# Revit family: PRD_AR_ShwrMxrs_SelfClosingShowerValve_F3SM2004
name_source: partatom
category: Plumbing Fixtures
revit_build: Autodesk Revit 2018 (Build: 20190510_1515(x64)
units: mm (PartAtom-declared; Revit-internal decimal feet)

## family parameters
Cut with Voids When Loaded = Yes
Host = Face
OmniClass Number = 23.45.05.14.99
OmniClass Title = Other Sanitary Washing Plumbing Fixtures
Part Type = Normal
Room Calculation Point = No
Round Connector Dimension = Use Diameter
Shared = No

## types (1)
- F3SM2004 with installation kit F3BX2001
    AssetType = Fixed
    BIMObjectName = PRD_AR_ShowerManualWaterSupplySets_SelfClosingShowerValve_F3SM2004
    BodyMaterial = Brass
    CasingMaterial = PRD_AR_StainlessSteel_SatinFinished
    Category = Pr_40_20_87_78, Shower manual water supply sets
    CloseOffRating = 0
    Color = Chrome
    Default Elevation = 1000 mm  [stored 3.28084 ft]
    Description = F3S-Mix self-closing single-mixer DN 15 as finished installation kit for installation in basic installation kit, for shower facilities. Self-closing mixing cartridge, hydraulically controlled, piston-free design, self-closing, stepless configuration of flow duration. With adjustable temperature stop. Connects to hot and cold water. All-metal construction, visible parts high-polished, chromium-plated. Holding frame including profile seal, stainless steel cover plate 190 x 245 mm with covered screw fixing, chromium-plated plastic rosettes, backflow preventer and strainers. Depth adjustability 25 mm.
    DiameterNominal = 15  [stored 0.0492126 ft]
    DurationUnit = year
    Finish = Chromised
    FittingMaterial = PRD_AR_ChromatedBrass_HighPolished
    FlowCoefficient = 0
    FlowColdWater = 0.2 L/s
    FlowHotWater = 0.2 L/s
    FunctionalPrinciple = HYDRALIC-C
    GrossWeight = 2.92 kg
    IfcExportAs = IfcValveType
    IfcExportType = MIXING
    Manufacturer = KWC Group AG
    ManufacturerName = KWC Group AG
    ManufacturerURL = www.kwc.com
    Material = Brass
    MaterialsBody = Brass
    MaterialsFinishAndColour = Chrome
    MaximumFlowTime = 35s
    MinimumFlowPressure = 1.00 bar
    MinimumFlowTime = 5s
    MixerControl = Other
    Model = F3SM2004
    ModelNumber = 2030040074
    ModelReference = F3SM2004
    NBSDescription = Shower mixers
    NBSReference = 45-35-70/335
    Name = F3 Self closing shower valve F3SM2004
    NetWeight = 2.78 kg
    NominalHeight = 0 mm  [stored 0 ft]
    NominalLength = 0 mm  [stored 0 ft]
    NominalWidth = 0 mm  [stored 0 ft]
    OutletConnectionSize = 15  [stored 0.0492126 ft]
    ProductInformation = https://pim.kwc.com
    Size = 15 mm  [stored 0.0492126 ft]
    TestPressure = 0
    TypeOfMounting = In-Wall-Installation-With-Box
    TypeOfShower = In-Wall-Fitting
    URL = www.kwc.com
    Uniclass2015Code = Pr_40_20_87_78
    Uniclass2015Title = Shower manual water supply sets
    Uniclass2015Version = Products v1.10
    ValveMechanism = Other
    ValveOperation = Other
    Version = 1
    VolumeFlowRateAt3Bar = 0.25 L/s
    WarrantyDurationUnit = year

note: [stored X ft] marks values corroborated as IEEE doubles in the binary element streams (Revit-internal decimal feet)

## geometry (parser evidence)
native form markers: Sweep x4
no freeform markers — native parametric forms only
